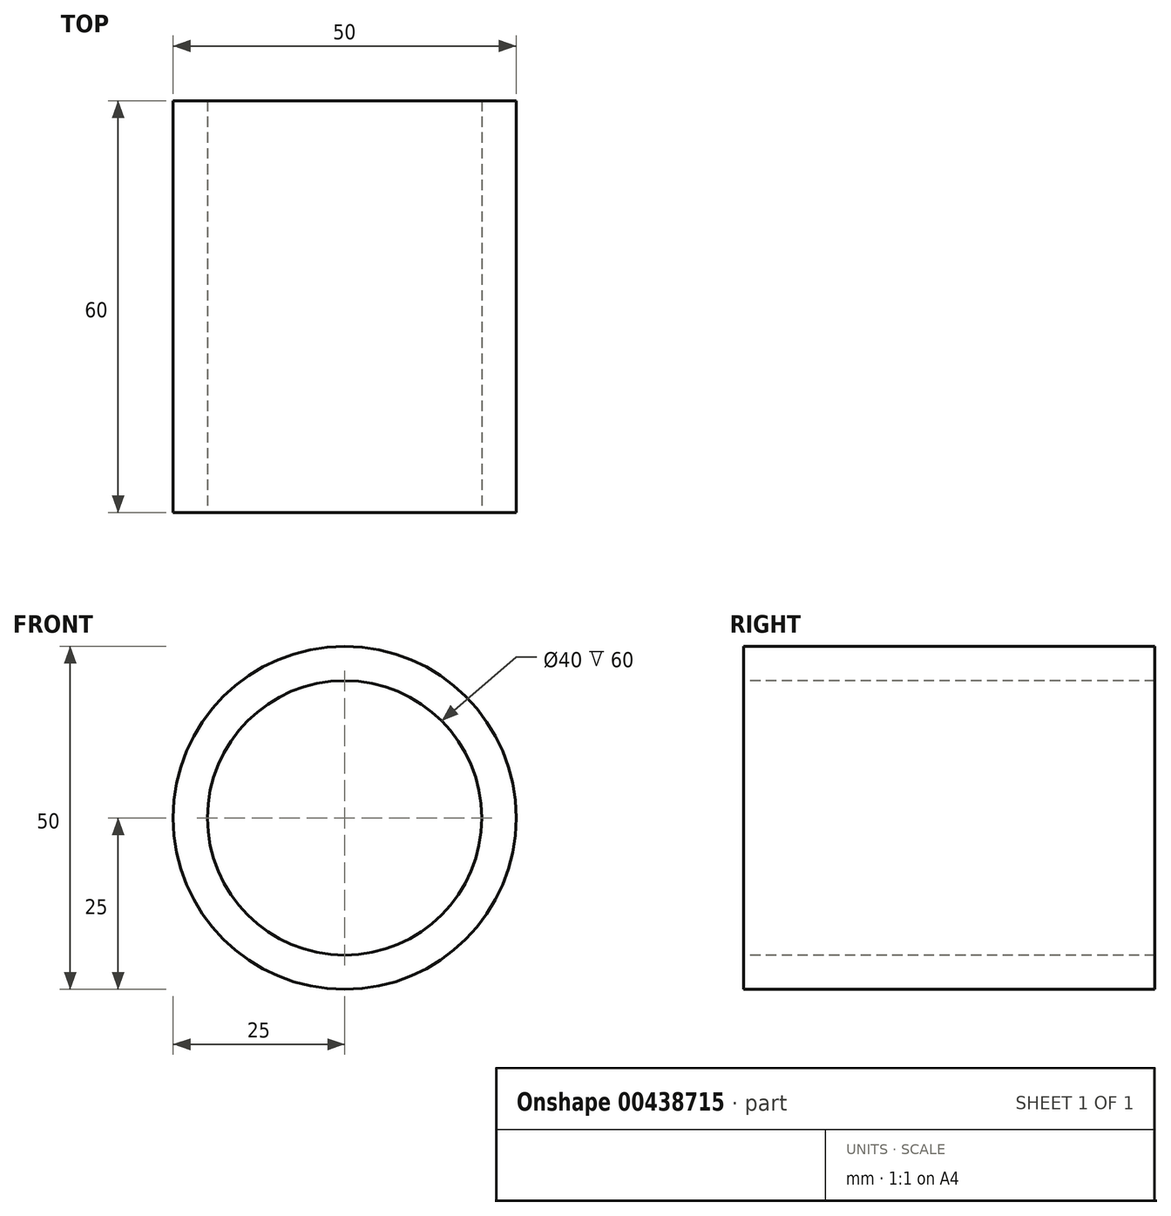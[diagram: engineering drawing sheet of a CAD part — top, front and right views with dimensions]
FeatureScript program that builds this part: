
annotation { "Feature Type Name" : "Feature", "Feature Type Description" : "" }
export const myFeature = defineFeature(function(context is Context, id is Id, definition is map)
    precondition{}
    {
        {
            var Q0;
            Q0=qCreatedBy(makeId("Right.planeOp"),FACE);
            var sketch = newSketch(context, id + "F0", { "sketchPlane" : qUnion([Q0])});
            skLineSegment(sketch, "E0", {"start": v(0, 0) * mm, "end": v(60, 0) * mm, "construction": true});
            skLineSegment(sketch, "E1.bottom", {"start": v(0, 25) * mm, "end": v(60, 25) * mm});
            skLineSegment(sketch, "E1.top", {"start": v(0, 20) * mm, "end": v(60, 20) * mm});
            skLineSegment(sketch, "E1.left", {"start": v(0, 25) * mm, "end": v(0, 20) * mm});
            skLineSegment(sketch, "E1.right", {"start": v(60, 25) * mm, "end": v(60, 20) * mm});
            skLineSegment(sketch, "E2.MirrorCS", {"start": v(0, -25) * mm, "end": v(60, -25) * mm});
            skLineSegment(sketch, "E3.MirrorCS", {"start": v(60, -25) * mm, "end": v(60, -20) * mm});
            skLineSegment(sketch, "E4.MirrorCS", {"start": v(0, -20) * mm, "end": v(60, -20) * mm});
            skLineSegment(sketch, "E5.MirrorCS", {"start": v(0, -25) * mm, "end": v(0, -20) * mm});
            skSolve(sketch);
        }
        {
            var Q0;
            Q0=makeQuery(id+"F0.imprint","IMPRINT",FACE,{"disambiguationData":[TD([[makeQuery(id+"F0.imprint","IMPRINT",EDGE,{"derivedFrom":sQuery(id+"F0.wireOp",EDGE,"E1.bottom")}),-1.0]])]});
            var Q1;
            Q1=sQuery(id+"F0.wireOp",EDGE,"E0");
            revolve(context, id + "F1", {"entities" : qUnion([Q0]), "axis" : qUnion([Q1]), "revolveType" : RevolveType.FULL});
        }
    });
